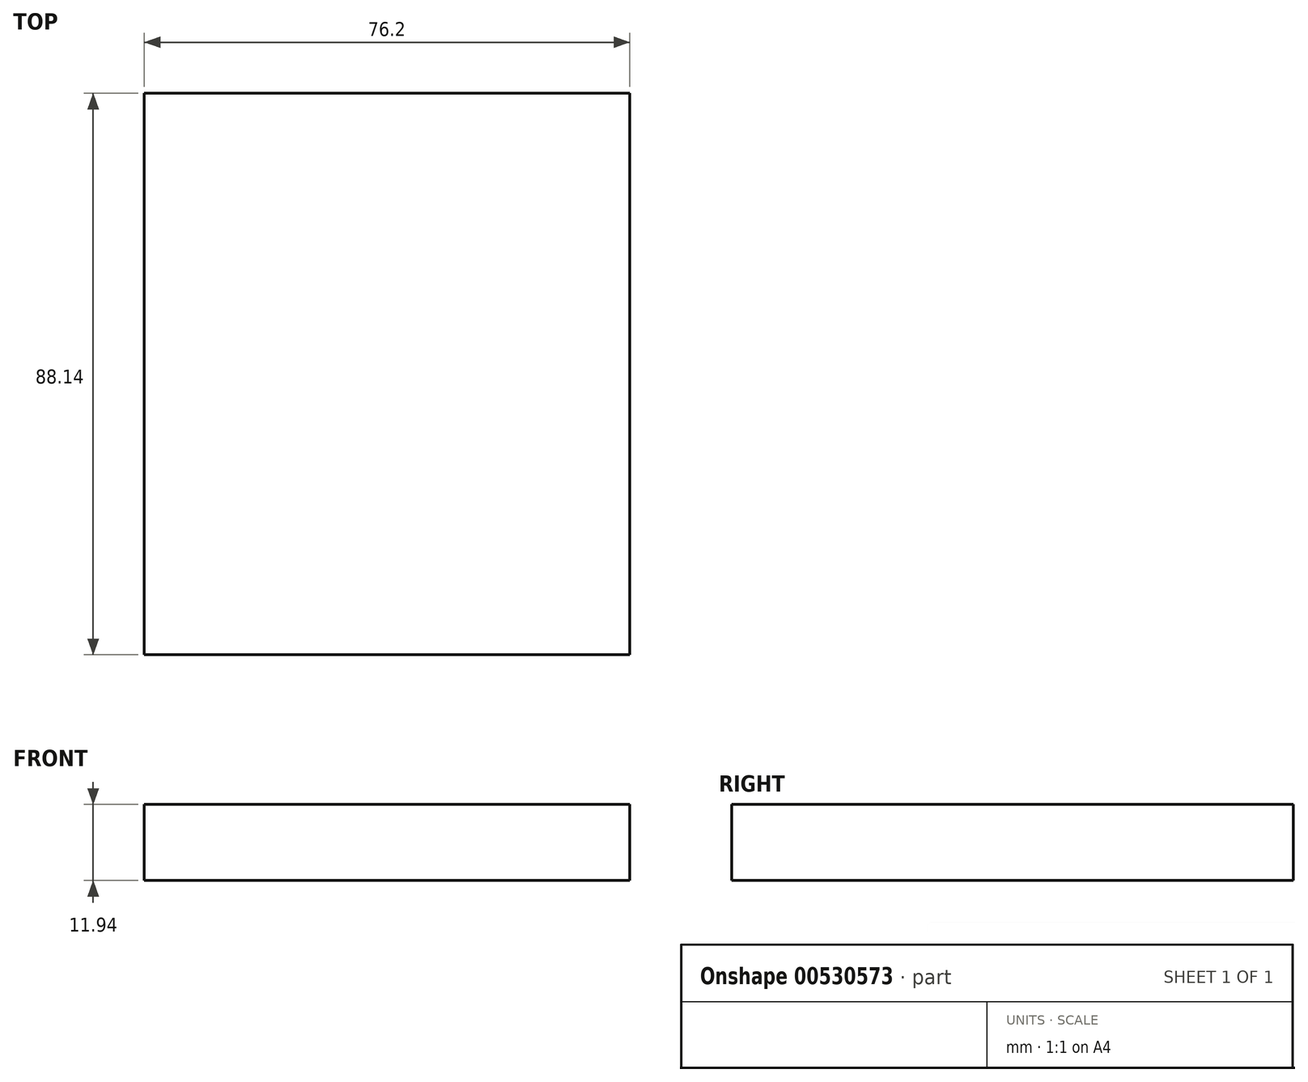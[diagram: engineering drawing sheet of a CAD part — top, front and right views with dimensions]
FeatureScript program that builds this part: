
annotation { "Feature Type Name" : "Feature", "Feature Type Description" : "" }
export const myFeature = defineFeature(function(context is Context, id is Id, definition is map)
    precondition{}
    {
        {
            var Q0;
            Q0=qCreatedBy(makeId("Top.planeOp"),FACE);
            var sketch = newSketch(context, id + "F0", { "sketchPlane" : qUnion([Q0])});
            skLineSegment(sketch, "E0.bottom", {"start": v(0, 0) * mm, "end": v(76.2, 0) * mm});
            skLineSegment(sketch, "E0.top", {"start": v(0, -88.14) * mm, "end": v(76.2, -88.14) * mm});
            skLineSegment(sketch, "E0.left", {"start": v(0, 0) * mm, "end": v(0, -88.14) * mm});
            skLineSegment(sketch, "E0.right", {"start": v(76.2, 0) * mm, "end": v(76.2, -88.14) * mm});
            skSolve(sketch);
        }
        {
            var Q0;
            Q0 = qSketchRegion(id + "F0", true);
            extrude(context, id + "F1", {"entities" : qUnion([Q0]), "depth" : 11.94 * mm, "offsetDistance" : 25.4 * mm});
        }
    });
